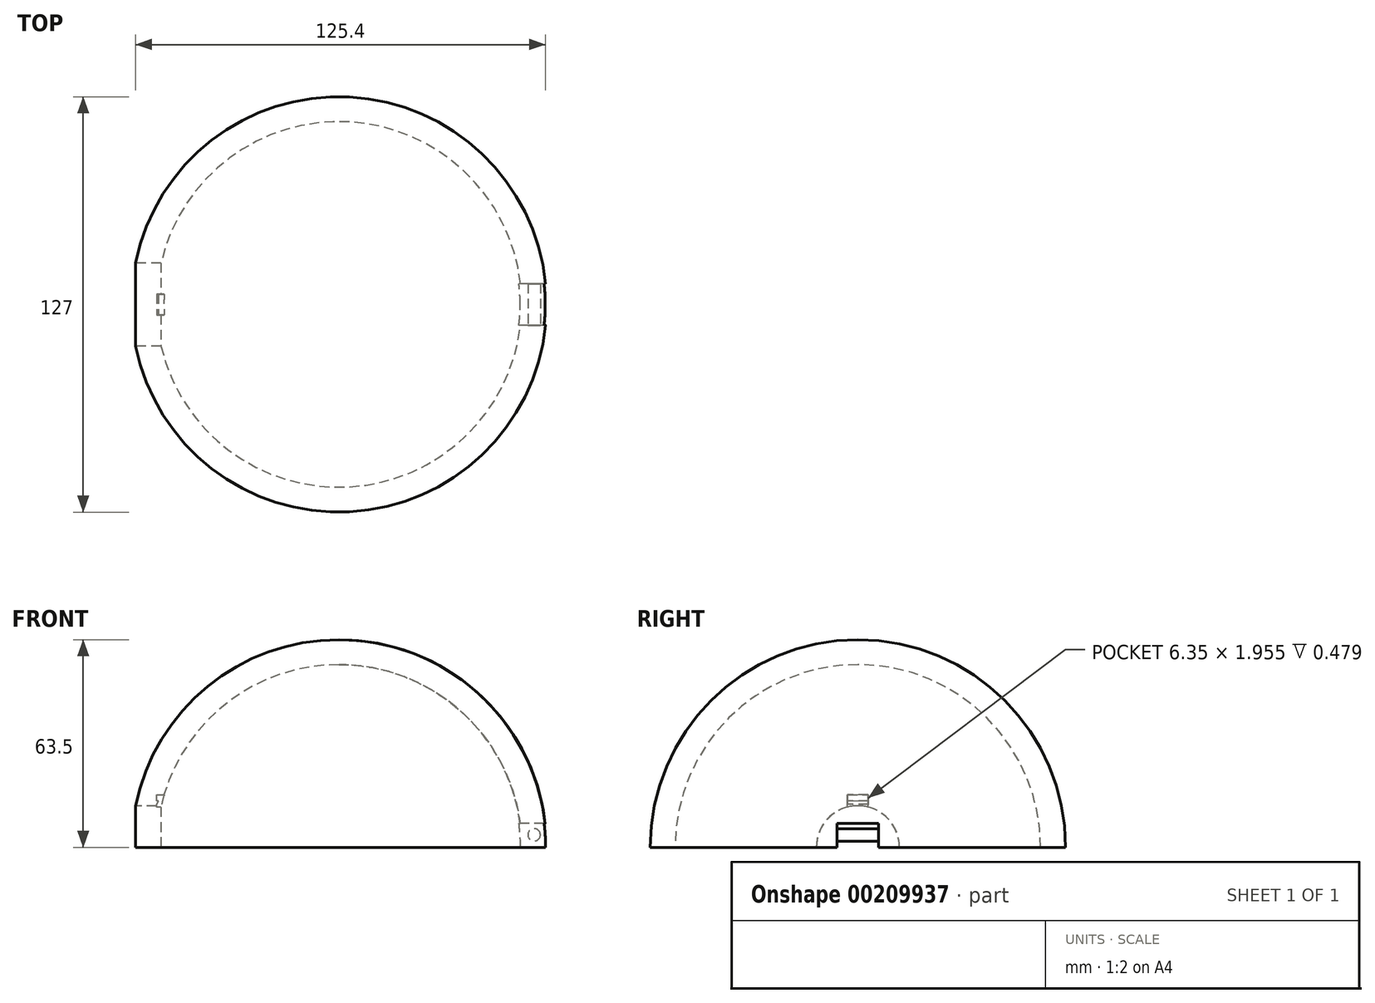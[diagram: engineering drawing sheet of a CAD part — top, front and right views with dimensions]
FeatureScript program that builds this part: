
annotation { "Feature Type Name" : "Feature", "Feature Type Description" : "" }
export const myFeature = defineFeature(function(context is Context, id is Id, definition is map)
    precondition{}
    {
        {
            var Q0;
            Q0=qCreatedBy(makeId("Front.planeOp"),FACE);
            var sketch = newSketch(context, id + "F0", { "sketchPlane" : qUnion([Q0])});
            skArc(sketch, "E0", {"start": v(63.5, 0) * mm, "mid": v(44.9, 44.9) * mm, "end": v(0, 63.5) * mm});
            skLineSegment(sketch, "E1", {"start": v(0, 55.88) * mm, "end": v(0, 63.5) * mm});
            skArc(sketch, "E2.0", {"start": v(55.88, 0) * mm, "mid": v(39.51, 39.51) * mm, "end": v(0, 55.88) * mm});
            skLineSegment(sketch, "E3.trimOffspring", {"start": v(55.88, 0) * mm, "end": v(63.5, 0) * mm});
            skPoint(sketch, "E4.start.orphan", {"position": v(-63.5, 0) * mm});
            skSolve(sketch);
        }
        {
            var Q0;
            Q0=makeQuery(id+"F0.imprint","IMPRINT",FACE,{"disambiguationData":[TD([[makeQuery(id+"F0.imprint","IMPRINT",EDGE,{"derivedFrom":sQuery(id+"F0.wireOp",EDGE,"E0")}),1.0]])]});
            var Q1;
            Q1=sQuery(id+"F0.wireOp",EDGE,"E1");
            revolve(context, id + "F1", {"entities" : qUnion([Q0]), "axis" : qUnion([Q1]), "revolveType" : RevolveType.FULL});
        }
        {
            var Q0;
            Q0=qCreatedBy(makeId("Right.planeOp"),FACE);
            cPlane(context, id + "F2", {"entities" : qUnion([Q0]), "cplaneType" : CPlaneType.OFFSET, "offset" : 63.5 * mm, "oppositeDirection" : true, "width" : 152.4 * mm, "height" : 152.4 * mm});
        }
        {
            var Q0;
            Q0=qCreatedBy(id+"F2.planeOp",FACE);
            var sketch = newSketch(context, id + "F3", { "sketchPlane" : qUnion([Q0])});
            skCircle(sketch, "E5", {"center": v(0, 0) * mm, "radius": 12.7 * mm});
            skSolve(sketch);
        }
        {
            var Q0;
            Q0=makeQuery(id+"F3.imprint","IMPRINT",FACE,{"disambiguationData":[TD([[makeQuery(id+"F3.imprint","IMPRINT",EDGE,{"derivedFrom":sQuery(id+"F3.wireOp",EDGE,"E5")}),1.0]])]});
            extrude(context, id + "F4", {"entities" : qUnion([Q0]), "operationType" : NewBodyOperationType.REMOVE, "depth" : 25.4 * mm});
        }
        {
            var Q0;
            Q0=qCreatedBy(makeId("Front.planeOp"),FACE);
            var sketch = newSketch(context, id + "F5", { "sketchPlane" : qUnion([Q0])});
            skCircle(sketch, "E6", {"center": v(59.69, 3.8) * mm, "radius": 1.9 * mm});
            skPoint(sketch, "E6.centerSnap0", {"position": v(59.69, 0) * mm});
            skLineSegment(sketch, "E7", {"start": v(49.01, -0.32) * mm, "end": v(48.06, 0.36) * mm});
            skLineSegment(sketch, "E8", {"start": v(48.06, 0.36) * mm, "end": v(53, 7.3) * mm});
            skLineSegment(sketch, "E9", {"start": v(49.01, -0.32) * mm, "end": v(63.5, 0) * mm, "construction": true});
            skLineSegment(sketch, "E10", {"start": v(63.5, 0) * mm, "end": v(63.5, 7.3) * mm, "construction": true});
            skLineSegment(sketch, "E11", {"start": v(63.5, 7.3) * mm, "end": v(53, 7.3) * mm});
            skArc(sketch, "E12", {"start": v(63.5, 0) * mm, "mid": v(6.38, 63.18) * mm, "end": v(-62.22, 12.7) * mm, "construction": true});
            skLineSegment(sketch, "E13", {"start": v(49.01, -0.32) * mm, "end": v(63.92, -0.69) * mm});
            skLineSegment(sketch, "E14", {"start": v(63.92, -0.69) * mm, "end": v(65.91, 6.5) * mm});
            skLineSegment(sketch, "E15", {"start": v(65.91, 6.5) * mm, "end": v(63.5, 7.3) * mm});
            skSolve(sketch);
        }
        {
            var Q0;
            Q0=makeQuery(id+"F5.imprint","IMPRINT",FACE,{"disambiguationData":[TD([[makeQuery(id+"F5.imprint","IMPRINT",EDGE,{"derivedFrom":sQuery(id+"F5.wireOp",EDGE,"E6")}),-1.0]])]});
            extrude(context, id + "F6", {"entities" : qUnion([Q0]), "operationType" : NewBodyOperationType.REMOVE, "endBound" : BoundingType.SYMMETRIC, "oppositeDirection" : true, "depth" : 12.7 * mm});
        }
        {
            var Q0;
            Q0=qCreatedBy(makeId("Front.planeOp"),FACE);
            var sketch = newSketch(context, id + "F7", { "sketchPlane" : qUnion([Q0])});
            skLineSegment(sketch, "E16", {"start": v(-54.55, 12.05) * mm, "end": v(-55.75, 12.05) * mm});
            skLineSegment(sketch, "E17", {"start": v(-55.75, 12.05) * mm, "end": v(-55.75, 13.11) * mm});
            skLineSegment(sketch, "E18", {"start": v(-55.75, 13.11) * mm, "end": v(-55.2, 14) * mm});
            skLineSegment(sketch, "E19", {"start": v(-55.27, 14.13) * mm, "end": v(-55.75, 14.13) * mm});
            skLineSegment(sketch, "E20", {"start": v(-55.75, 14.13) * mm, "end": v(-55.75, 16.09) * mm});
            skLineSegment(sketch, "E21", {"start": v(-55.75, 16.09) * mm, "end": v(-52.42, 16.09) * mm});
            skLineSegment(sketch, "E22", {"start": v(-52.42, 16.09) * mm, "end": v(-53.66, 11.97) * mm});
            skLineSegment(sketch, "E23", {"start": v(-53.66, 11.97) * mm, "end": v(-54.55, 12.05) * mm});
            skPoint(sketch, "E24.visualSharp", {"position": v(-55.12, 14.13) * mm});
            skArc(sketch, "E24.filletArc", {"start": v(-55.2, 14) * mm, "mid": v(-55.2, 14.09) * mm, "end": v(-55.27, 14.13) * mm});
            skSolve(sketch);
        }
        {
            var Q0;
            Q0 = qSketchRegion(id + "F7", true);
            extrude(context, id + "F8", {"entities" : qUnion([Q0]), "operationType" : NewBodyOperationType.REMOVE, "endBound" : BoundingType.SYMMETRIC, "oppositeDirection" : true, "depth" : 6.35 * mm});
        }
    });
